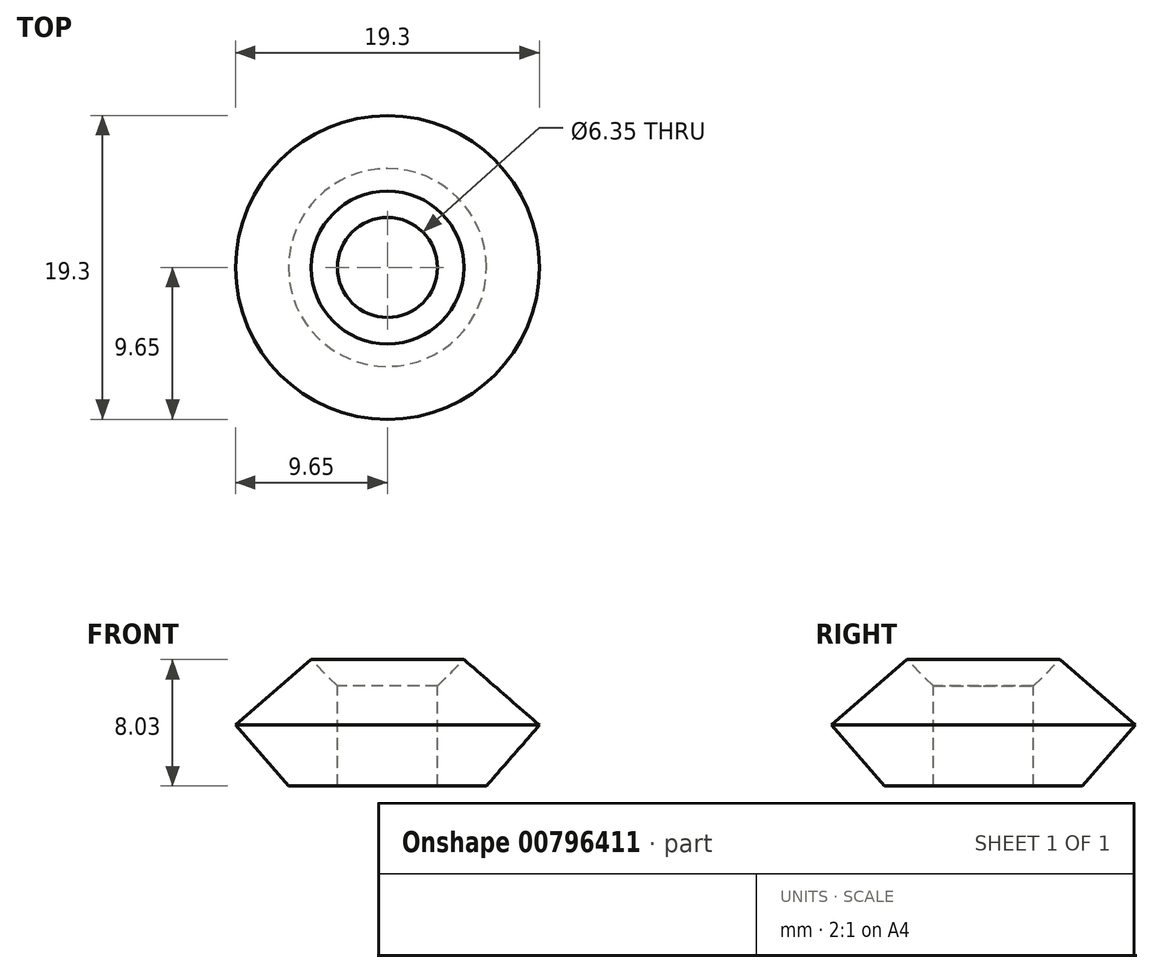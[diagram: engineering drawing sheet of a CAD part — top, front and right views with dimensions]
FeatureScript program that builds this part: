
annotation { "Feature Type Name" : "Feature", "Feature Type Description" : "" }
export const myFeature = defineFeature(function(context is Context, id is Id, definition is map)
    precondition{}
    {
        {
            var Q0;
            Q0=qCreatedBy(makeId("Front.planeOp"),FACE);
            var sketch = newSketch(context, id + "F0", { "sketchPlane" : qUnion([Q0])});
            skLineSegment(sketch, "E0", {"start": v(-3.18, 1.82) * mm, "end": v(-4.86, 3.5) * mm});
            skLineSegment(sketch, "E1", {"start": v(-4.86, 3.5) * mm, "end": v(-9.65, -0.67) * mm});
            skLineSegment(sketch, "E2", {"start": v(-9.65, -0.67) * mm, "end": v(-6.28, -4.53) * mm});
            skLineSegment(sketch, "E3", {"start": v(-6.28, -4.53) * mm, "end": v(-3.18, -4.53) * mm});
            skLineSegment(sketch, "E4", {"start": v(-3.18, 1.82) * mm, "end": v(-3.18, -4.53) * mm});
            skLineSegment(sketch, "E5", {"start": v(0, 0) * mm, "end": v(0, 3.9) * mm, "construction": true});
            skSolve(sketch);
        }
        {
            var Q0;
            Q0 = qConstructionFilter(qBodyType(qCreatedBy(id + "F0" ,EDGE), BodyType.WIRE), ConstructionObject.NO);
            var Q1;
            Q1=sQuery(id+"F0.wireOp",EDGE,"E5");
            revolve(context, id + "F1", {"bodyType" : ToolBodyType.SURFACE, "surfaceOperationType" : NewSurfaceOperationType.NEW, "surfaceEntities" : qUnion([Q0]), "axis" : qUnion([Q1]), "revolveType" : RevolveType.FULL});
        }
        {
            var Q0;
            Q0=sQuery(id+"F0.wireOp",EDGE,"E0");
            cPlane(context, id + "F2", {"entities" : qUnion([Q0]), "cplaneType" : CPlaneType.LINE_ANGLE, "offset" : 25.4 * mm, "angle" : 90 * degree, "width" : 152.4 * mm, "height" : 152.4 * mm});
        }
        {
            var Q0;
            Q0=qCreatedBy(id+"F2.planeOp",FACE);
            var sketch = newSketch(context, id + "F3", { "sketchPlane" : qUnion([Q0])});
            skLineSegment(sketch, "E6", {"start": v(-5.91, -0.8) * mm, "end": v(-4.72, -0.8) * mm});
            skLineSegment(sketch, "E7", {"start": v(-4.72, -0.8) * mm, "end": v(-3.93, -0.34) * mm});
            skSolve(sketch);
        }
        {
            var Q0;
            Q0=sQuery(id+"F3.wireOp",VERTEX,"E7.end");
            var Q1;
            Q1=sQuery(id+"F0.wireOp",EDGE,"E0");
            cPlane(context, id + "F4", {"entities" : qUnion([Q0, Q1]), "cplaneType" : CPlaneType.LINE_POINT, "offset" : 25.4 * mm, "width" : 152.4 * mm, "height" : 152.4 * mm});
        }
    });
